# Revit family: Crealco Palace OXXXXO
name_source: partatom
category: Doors
revit_build: Autodesk Revit 2016 (Build: 20150714_1515(x64)
units: mm (PartAtom-declared; Revit-internal decimal feet)

## family parameters
Always vertical = Yes
Cut with Voids When Loaded = No
Host = Wall
OmniClass Number = 23.30.20.00
OmniClass Title = Windows
Room Calculation Point = No
Shared = No

## types (19) — shared parameters
Description = High Performance Sliding Door
Limit Glazing Thickness Max = 25 mm  [stored 0.082021 ft]
Limit Glazing Thickness Min = 6 mm  [stored 0.019685 ft]
Limit Sash Height Max = 2400 mm
Limit Sash Height Min = 300 mm  [stored 0.984252 ft]
Limit Sash Width Max = 1500 mm  [stored 4.92126 ft]
Limit Sash Width Min = 300 mm  [stored 0.984252 ft]
Limit Window Height Max = 2459 mm
Limit Window Height Min = 359 mm  [stored 1.17782 ft]
Limit Window Width Max = 8906 mm
Limit Window Width Min = 1706 mm
Manufacturer = Crealco
Max Wind Load = 10000
Model = Palace
Sash Bottom Gap = 31 mm  [stored 0.101706 ft]
Sash Side Gap = 33 mm  [stored 0.108268 ft]
Sash Top Gap = 28 mm  [stored 0.0918635 ft]
Standard Astragal Ix = 25.113
Standard Interlock Ix = 25.866
URL = https://www.crealco.co.za
Wall Closure = By host
zero-valued in all types: Default Sill Height, Min Wind Load

## per-type parameters (varying)
| type | Standard Height | Standard Size | Standard Width | Type Comments |
| 4190 x 2090mm (Palace-4221OXXXXO) | 2090 mm  [stored 6.85696 ft] | Yes | 4190 mm  [stored 13.7467 ft] | Palace-4221OXXXXO |
| User Defined | 2090 mm  [stored 6.85696 ft] | No | 4190 mm  [stored 13.7467 ft] | Custom |
| 4790 x 2090mm (Palace-4821OXXXXO) | 2090 mm  [stored 6.85696 ft] | Yes | 4790 mm  [stored 15.7152 ft] | Palace-4821OXXXXO |
| 5390 x 2090mm (Palace-5421OXXXXO) | 2090 mm  [stored 6.85696 ft] | Yes | 5390 mm  [stored 17.6837 ft] | Palace-5421OXXXXO |
| 5990 x 2090mm (Palace-6021OXXXXO) | 2090 mm  [stored 6.85696 ft] | Yes | 5990 mm  [stored 19.6522 ft] | Palace-6021OXXXXO |
| 6590 x 2090mm (Palace-6621OXXXXO) | 2090 mm  [stored 6.85696 ft] | Yes | 6590 mm  [stored 21.6207 ft] | Palace-6621OXXXXO |
| 7190 x 2090mm (Palace-7221OXXXXO) | 2090 mm  [stored 6.85696 ft] | Yes | 7190 mm | Palace-7221OXXXXO |
| 7790 x 2090mm (Palace-7821OXXXXO) | 2090 mm  [stored 6.85696 ft] | Yes | 7790 mm | Palace-7821OXXXXO |
| 8390 x 2090mm (Palace-8421OXXXXO) | 2090 mm  [stored 6.85696 ft] | Yes | 8390 mm | Palace-8421OXXXXO |
| 8990 x 2090mm (Palace-9021OXXXXO) | 2090 mm  [stored 6.85696 ft] | Yes | 8990 mm | Palace-9021OXXXXO |
| 4190 x 2390mm (Palace-4224OXXXXO) | 2390 mm  [stored 7.84121 ft] | Yes | 4190 mm  [stored 13.7467 ft] | Palace-4224OXXXXO |
| 4790 x 2390mm (Palace-4824OXXXXO) | 2390 mm  [stored 7.84121 ft] | Yes | 4790 mm  [stored 15.7152 ft] | Palace-4824OXXXXO |
| 5390 x 2390mm (Palace-5424OXXXXO) | 2390 mm  [stored 7.84121 ft] | Yes | 5390 mm  [stored 17.6837 ft] | Palace-5424OXXXXO |
| 5990 x 2390mm (Palace-6024OXXXXO) | 2390 mm  [stored 7.84121 ft] | Yes | 5990 mm  [stored 19.6522 ft] | Palace-6024OXXXXO |
| 6590 x 2390mm (Palace-6624OXXXXO) | 2390 mm  [stored 7.84121 ft] | Yes | 6590 mm  [stored 21.6207 ft] | Palace-6624OXXXXO |
| 7190 x 2390mm (Palace-7224OXXXXO) | 2390 mm  [stored 7.84121 ft] | Yes | 7190 mm | Palace-7224OXXXXO |
| 7790 x 2390mm (Palace-7824OXXXXO) | 2390 mm  [stored 7.84121 ft] | Yes | 7790 mm | Palace-7824OXXXXO |
| 8390 x 2390mm (Palace-8424OXXXXO) | 2390 mm  [stored 7.84121 ft] | Yes | 8390 mm | Palace-8424OXXXXO |
| 8990 x 2390mm (Palace-9024OXXXXO) | 2390 mm  [stored 7.84121 ft] | Yes | 8990 mm | Palace-9024OXXXXO |

note: [stored X ft] marks values corroborated as IEEE doubles in the binary element streams (Revit-internal decimal feet)

## geometry (parser evidence)
native form markers: Sweep x36
no freeform markers — native parametric forms only
